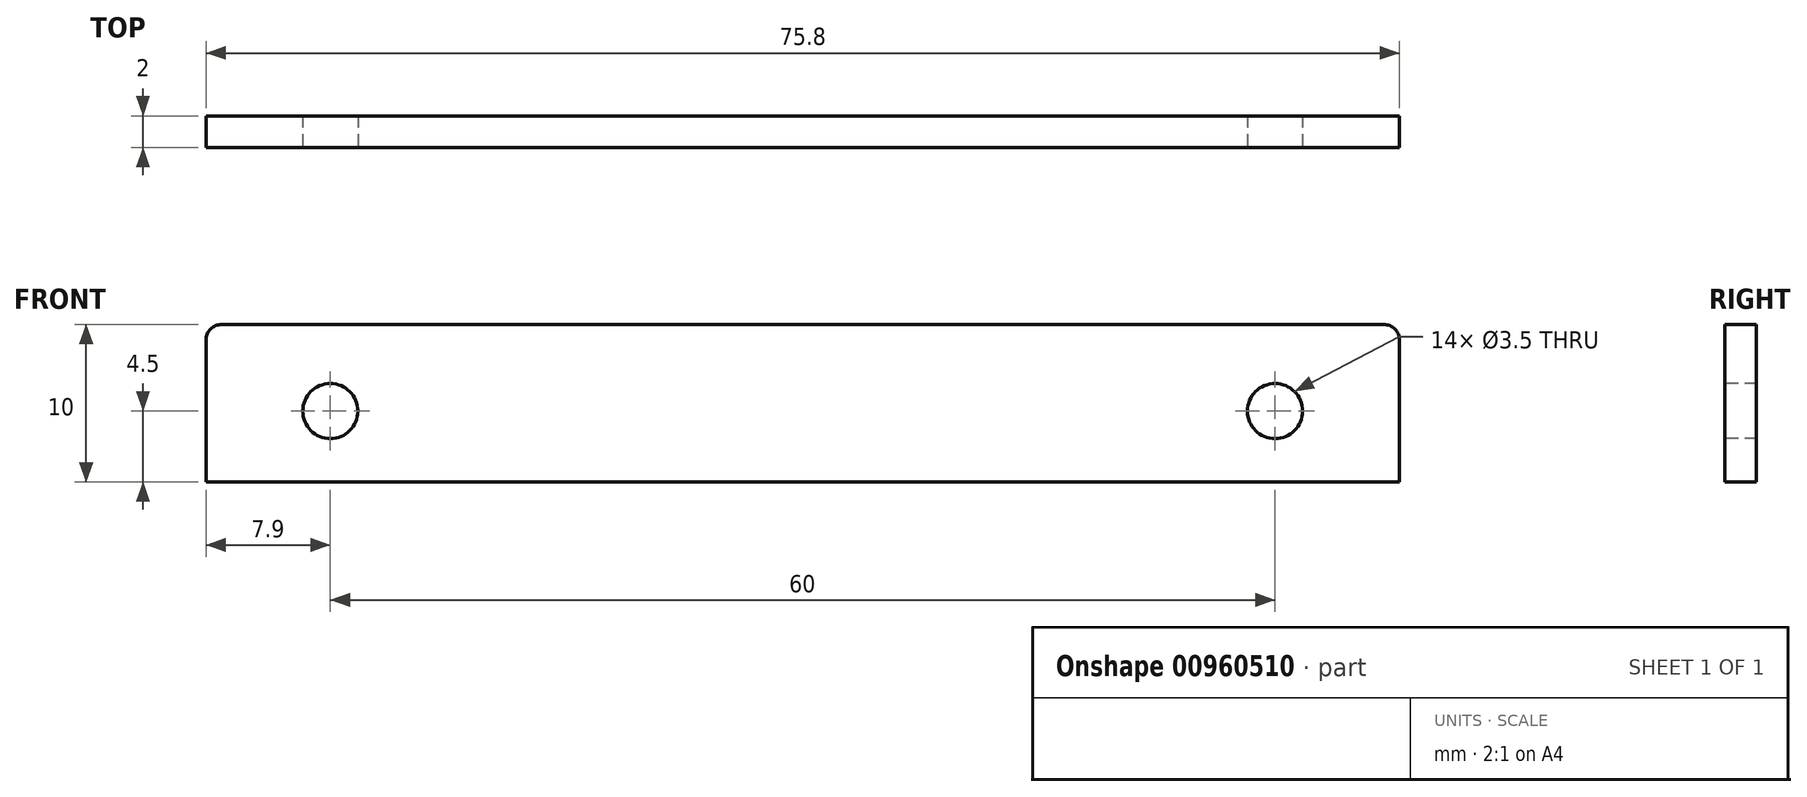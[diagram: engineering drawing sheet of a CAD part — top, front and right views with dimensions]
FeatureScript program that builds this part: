
annotation { "Feature Type Name" : "Feature", "Feature Type Description" : "" }
export const myFeature = defineFeature(function(context is Context, id is Id, definition is map)
    precondition{}
    {
        {
            var Q0;
            Q0=qCreatedBy(makeId("Front.planeOp"),FACE);
            var sketch = newSketch(context, id + "F0", { "sketchPlane" : qUnion([Q0])});
            skLineSegment(sketch, "E0.bottom", {"start": v(37.9, -5) * mm, "end": v(-37.9, -5) * mm});
            skLineSegment(sketch, "E0.top", {"start": v(37.9, 5) * mm, "end": v(-37.9, 5) * mm});
            skLineSegment(sketch, "E0.left", {"start": v(37.9, -5) * mm, "end": v(37.9, 5) * mm});
            skLineSegment(sketch, "E0.right", {"start": v(-37.9, -5) * mm, "end": v(-37.9, 5) * mm});
            skPoint(sketch, "E0.middle", {"position": v(0, 0) * mm});
            skSolve(sketch);
        }
        {
            var Q0;
            Q0=makeQuery(id+"F0.imprint","IMPRINT",FACE,{"disambiguationData":[TD([[makeQuery(id+"F0.imprint","IMPRINT",EDGE,{"derivedFrom":sQuery(id+"F0.wireOp",EDGE,"E0.bottom")}),-1.0]])]});
            extrude(context, id + "F1", {"entities" : qUnion([Q0]), "depth" : 2 * mm, "offsetDistance" : 25 * mm});
        }
        {
            var Q0;
            Q0=makeQuery(id+"F1.opExtrude","SWEPT_EDGE",EDGE,{"disambiguationData":[OSD([sQuery(id+"F0.wireOp",EDGE,"E0.top"),sQuery(id+"F0.wireOp",EDGE,"E0.right")])]});
            var Q1;
            Q1=makeQuery(id+"F1.opExtrude","SWEPT_EDGE",EDGE,{"disambiguationData":[OSD([sQuery(id+"F0.wireOp",EDGE,"E0.top"),sQuery(id+"F0.wireOp",EDGE,"E0.left")])]});
            fillet(context, id + "F2", {"entities" : qUnion([Q0, Q1]), "radius" : 1 * mm, "tangentPropagation" : true, "allowEdgeOverflow" : false});
        }
        {
            var Q0;
            Q0=makeQuery(id+"F1.opExtrude","CAP_FACE",FACE,{"disambiguationData":[OSD([sQuery(id+"F0.wireOp",EDGE,"E0.bottom"),sQuery(id+"F0.wireOp",EDGE,"E0.top"),sQuery(id+"F0.wireOp",EDGE,"E0.left"),sQuery(id+"F0.wireOp",EDGE,"E0.right")])],"isStart":false});
            var sketch = newSketch(context, id + "F3", { "sketchPlane" : qUnion([Q0])});
            skPoint(sketch, "E1", {"position": v(-30, -0.5) * mm});
            skPoint(sketch, "E2", {"position": v(30, -0.5) * mm});
            skPoint(sketch, "E3", {"position": v(53.9, -0.5) * mm});
            skSolve(sketch);
        }
        {
            var Q0;
            Q0=sQuery(id+"F3.wireOp",VERTEX,"E2");
            var Q1;
            Q1=sQuery(id+"F3.wireOp",VERTEX,"E1");
            var Q2;
            Q2=makeQuery(id+"F1.opExtrude","SWEPT_BODY",BODY,{"disambiguationData":[OSD([sQuery(id+"F0.wireOp",EDGE,"E0.bottom"),sQuery(id+"F0.wireOp",EDGE,"E0.top"),sQuery(id+"F0.wireOp",EDGE,"E0.left"),sQuery(id+"F0.wireOp",EDGE,"E0.right")])]});
            hole(context, id + "F4", {"style" : HoleStyle.SIMPLE, "endStyle" : HoleEndStyle.THROUGH, "standardTappedOrClearance" : lookupTablePath({ "standard" : "ISO", "size" : "3.5", "type" : "Drilled" }), "standardBlindInLast" : lookupTablePath({ "standard" : "ISO", "size" : "3.5", "type" : "Drilled" }), "holeDiameter" : 3.5 * mm, "majorDiameter" : 3 * mm, "isTappedThrough" : true, "tappedDepth" : 4 * mm, "tapClearance" : 3, "locations" : qUnion([Q0, Q1]), "scope" : qUnion([Q2])});
        }
    });
